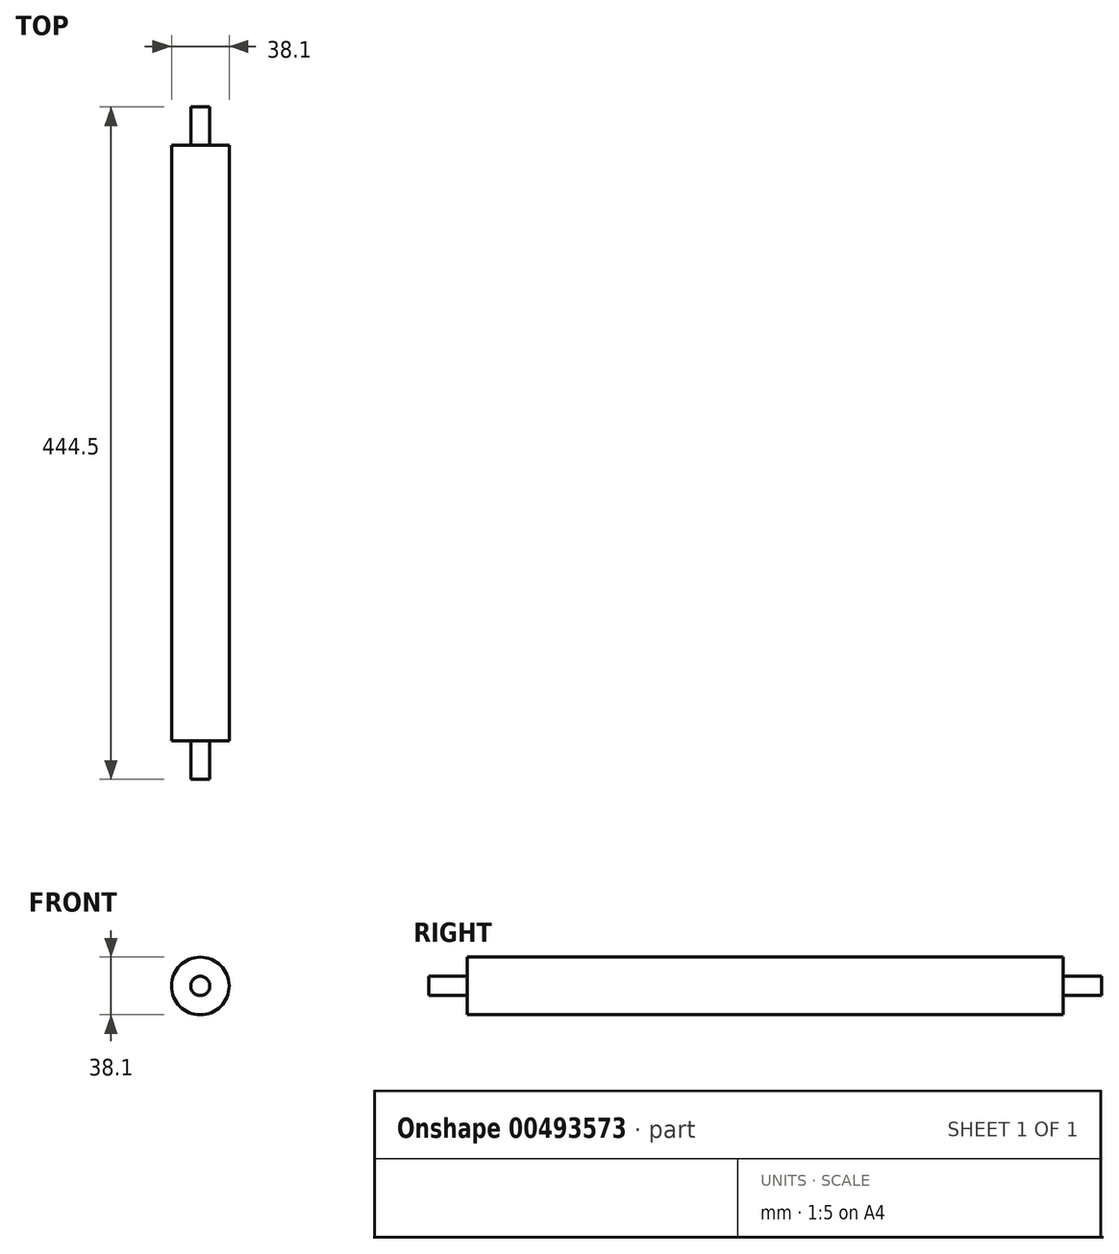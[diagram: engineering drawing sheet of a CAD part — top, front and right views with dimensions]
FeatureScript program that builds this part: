
annotation { "Feature Type Name" : "Feature", "Feature Type Description" : "" }
export const myFeature = defineFeature(function(context is Context, id is Id, definition is map)
    precondition{}
    {
        {
            var Q0;
            Q0=qCreatedBy(makeId("Front.planeOp"),FACE);
            var sketch = newSketch(context, id + "F0", { "sketchPlane" : qUnion([Q0])});
            skCircle(sketch, "E0", {"center": v(0, 0) * mm, "radius": 19.05 * mm});
            skSolve(sketch);
        }
        {
            var Q0;
            Q0=makeQuery(id+"F0.imprint","IMPRINT",FACE,{"disambiguationData":[TD([[makeQuery(id+"F0.imprint","IMPRINT",EDGE,{"derivedFrom":sQuery(id+"F0.wireOp",EDGE,"E0")}),1.0]])]});
            extrude(context, id + "F1", {"entities" : qUnion([Q0]), "endBound" : BoundingType.SYMMETRIC, "depth" : 393.7 * mm});
        }
        {
            var Q0;
            Q0=makeQuery(id+"F1.opExtrude","CAP_FACE",FACE,{"disambiguationData":[OSD([sQuery(id+"F0.wireOp",EDGE,"E0")])],"isStart":false});
            var sketch = newSketch(context, id + "F2", { "sketchPlane" : qUnion([Q0])});
            skCircle(sketch, "E1", {"center": v(0, 0) * mm, "radius": 6.35 * mm});
            skSolve(sketch);
        }
        {
            var Q0;
            Q0=makeQuery(id+"F2.imprint","IMPRINT",FACE,{"disambiguationData":[TD([[makeQuery(id+"F2.imprint","IMPRINT",EDGE,{"derivedFrom":sQuery(id+"F2.wireOp",EDGE,"E1")}),1.0]])]});
            extrude(context, id + "F3", {"entities" : qUnion([Q0]), "operationType" : NewBodyOperationType.ADD, "depth" : 25.4 * mm});
        }
        {
            var Q0;
            Q0=makeQuery(id+"F1.opExtrude","CAP_FACE",FACE,{"disambiguationData":[OSD([sQuery(id+"F0.wireOp",EDGE,"E0")])],"isStart":true});
            var sketch = newSketch(context, id + "F4", { "sketchPlane" : qUnion([Q0])});
            skCircle(sketch, "E2", {"center": v(0, 0) * mm, "radius": 6.35 * mm});
            skSolve(sketch);
        }
        {
            var Q0;
            Q0 = qSketchRegion(id + "F4", true);
            extrude(context, id + "F5", {"entities" : qUnion([Q0]), "operationType" : NewBodyOperationType.ADD, "depth" : 25.4 * mm});
        }
    });
